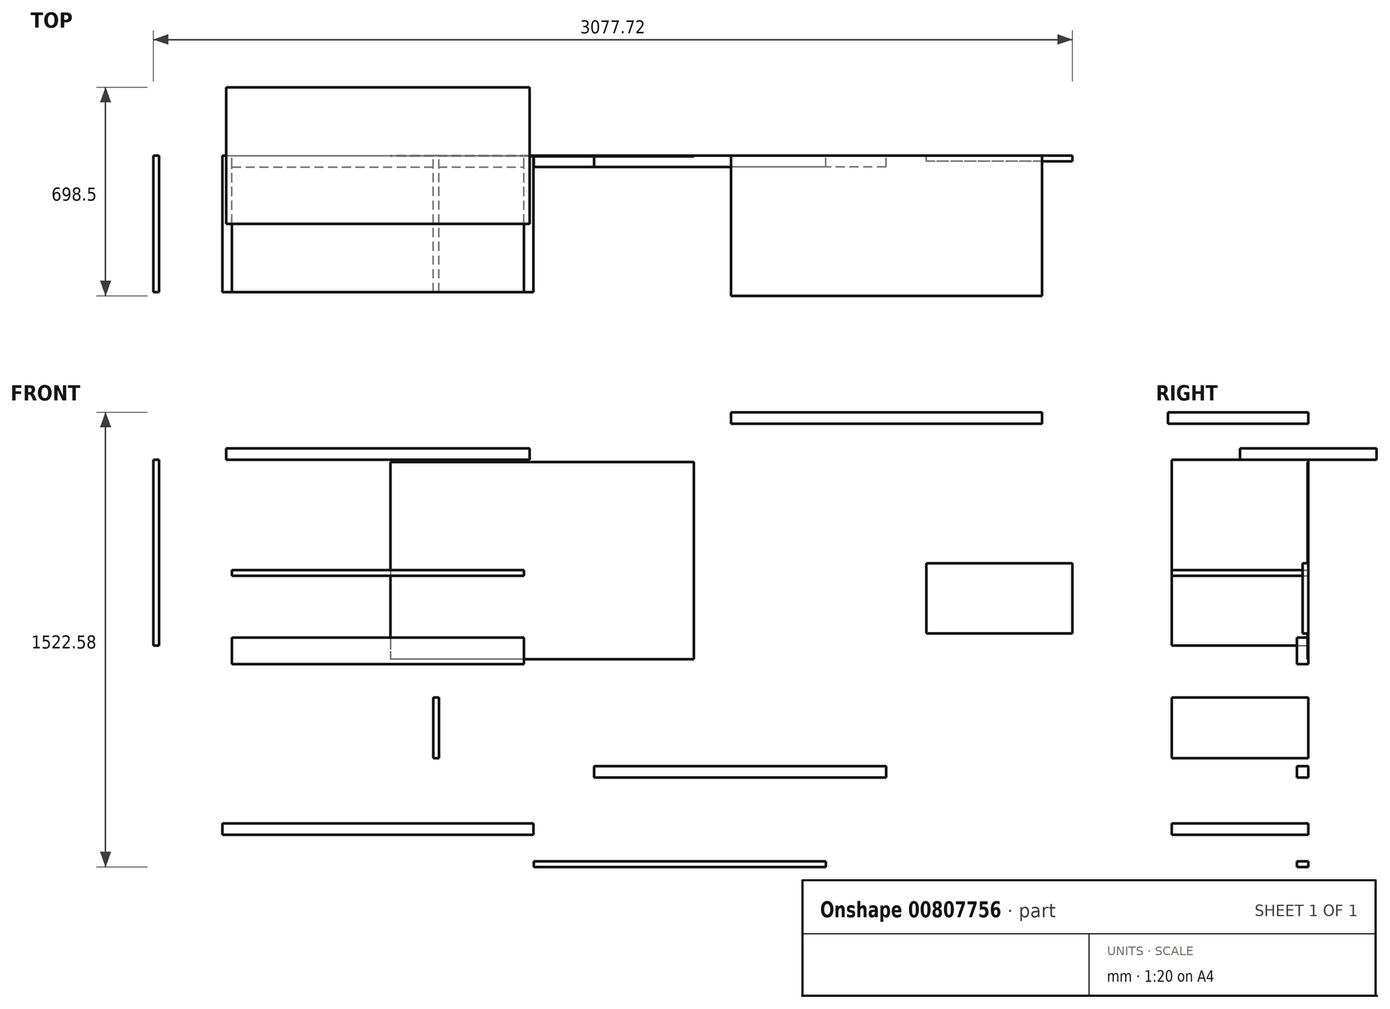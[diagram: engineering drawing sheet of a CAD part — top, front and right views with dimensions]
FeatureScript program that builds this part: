
annotation { "Feature Type Name" : "Feature", "Feature Type Description" : "" }
export const myFeature = defineFeature(function(context is Context, id is Id, definition is map)
    precondition{}
    {
        {
            var Q0;
            Q0=qCreatedBy(makeId("Top.planeOp"),FACE);
            var sketch = newSketch(context, id + "F0", { "sketchPlane" : qUnion([Q0])});
            skLineSegment(sketch, "E0.bottom", {"start": v(508, 228.6) * mm, "end": v(-508, 228.6) * mm});
            skLineSegment(sketch, "E0.top", {"start": v(508, -228.6) * mm, "end": v(-508, -228.6) * mm});
            skLineSegment(sketch, "E0.left", {"start": v(508, 228.6) * mm, "end": v(508, -228.6) * mm});
            skLineSegment(sketch, "E0.right", {"start": v(-508, 228.6) * mm, "end": v(-508, -228.6) * mm});
            skPoint(sketch, "E0.middle", {"position": v(0, 0) * mm});
            skSolve(sketch);
        }
        {
            var Q0;
            Q0 = qSketchRegion(id + "F0", true);
            extrude(context, id + "F1", {"entities" : qUnion([Q0]), "depth" : 38.1 * mm, "offsetDistance" : 25.4 * mm});
        }
        {
            var Q0;
            Q0=qCreatedBy(makeId("Front.planeOp"),FACE);
            var sketch = newSketch(context, id + "F2", { "sketchPlane" : qUnion([Q0])});
            skLineSegment(sketch, "E1.bottom", {"start": v(-752.27, 0) * mm, "end": v(-733.22, 0) * mm});
            skLineSegment(sketch, "E1.top", {"start": v(-752.27, -622.3) * mm, "end": v(-733.22, -622.3) * mm});
            skLineSegment(sketch, "E1.left", {"start": v(-752.27, 0) * mm, "end": v(-752.27, -622.3) * mm});
            skLineSegment(sketch, "E1.right", {"start": v(-733.22, 0) * mm, "end": v(-733.22, -622.3) * mm});
            skSolve(sketch);
        }
        {
            var Q0;
            Q0 = qSketchRegion(id + "F2", true);
            extrude(context, id + "F3", {"entities" : qUnion([Q0]), "depth" : 457.2 * mm, "offsetDistance" : 25.4 * mm});
        }
        {
            var Q0;
            Q0=qCreatedBy(makeId("Front.planeOp"),FACE);
            var sketch = newSketch(context, id + "F4", { "sketchPlane" : qUnion([Q0])});
            skLineSegment(sketch, "E2.bottom", {"start": v(-488.95, -369.1) * mm, "end": v(488.95, -369.1) * mm});
            skLineSegment(sketch, "E2.top", {"start": v(-488.95, -388.14) * mm, "end": v(488.95, -388.14) * mm});
            skLineSegment(sketch, "E2.left", {"start": v(-488.95, -369.1) * mm, "end": v(-488.95, -388.14) * mm});
            skLineSegment(sketch, "E2.right", {"start": v(488.95, -369.1) * mm, "end": v(488.95, -388.14) * mm});
            skPoint(sketch, "E2.middle", {"position": v(0, -378.62) * mm});
            skSolve(sketch);
        }
        {
            var Q0;
            Q0 = qSketchRegion(id + "F4", true);
            extrude(context, id + "F5", {"entities" : qUnion([Q0]), "depth" : 457.2 * mm, "offsetDistance" : 25.4 * mm});
        }
        {
            var Q0;
            Q0=qCreatedBy(makeId("Front.planeOp"),FACE);
            var sketch = newSketch(context, id + "F6", { "sketchPlane" : qUnion([Q0])});
            skLineSegment(sketch, "E3.bottom", {"start": v(-488.95, -595.4) * mm, "end": v(488.95, -595.4) * mm});
            skLineSegment(sketch, "E3.top", {"start": v(-488.95, -684.3) * mm, "end": v(488.95, -684.3) * mm});
            skLineSegment(sketch, "E3.left", {"start": v(-488.95, -595.4) * mm, "end": v(-488.95, -684.3) * mm});
            skLineSegment(sketch, "E3.right", {"start": v(488.95, -595.4) * mm, "end": v(488.95, -684.3) * mm});
            skPoint(sketch, "E3.middle", {"position": v(0, -639.85) * mm});
            skSolve(sketch);
        }
        {
            var Q0;
            Q0 = qSketchRegion(id + "F6", true);
            extrude(context, id + "F7", {"entities" : qUnion([Q0]), "depth" : 38.1 * mm, "offsetDistance" : 25.4 * mm});
        }
        {
            var Q0;
            Q0=qCreatedBy(makeId("Front.planeOp"),FACE);
            var sketch = newSketch(context, id + "F8", { "sketchPlane" : qUnion([Q0])});
            skLineSegment(sketch, "E4.bottom", {"start": v(1057.42, -7.03) * mm, "end": v(41.42, -7.03) * mm});
            skLineSegment(sketch, "E4.top", {"start": v(1057.42, -667.43) * mm, "end": v(41.42, -667.43) * mm});
            skLineSegment(sketch, "E4.left", {"start": v(1057.42, -7.03) * mm, "end": v(1057.42, -667.43) * mm});
            skLineSegment(sketch, "E4.right", {"start": v(41.42, -7.03) * mm, "end": v(41.42, -667.43) * mm});
            skPoint(sketch, "E4.middle", {"position": v(549.42, -337.23) * mm});
            skSolve(sketch);
        }
        {
            var Q0;
            Q0=makeQuery(id+"F8.imprint","IMPRINT",FACE,{"disambiguationData":[TD([[makeQuery(id+"F8.imprint","IMPRINT",EDGE,{"derivedFrom":sQuery(id+"F8.wireOp",EDGE,"E4.bottom")}),1.0]])]});
            extrude(context, id + "F9", {"entities" : qUnion([Q0]), "depth" : 2.54 * mm, "offsetDistance" : 25.4 * mm});
        }
        {
            var Q0;
            Q0=qCreatedBy(makeId("Front.planeOp"),FACE);
            var sketch = newSketch(context, id + "F10", { "sketchPlane" : qUnion([Q0])});
            skLineSegment(sketch, "E5.bottom", {"start": v(203.4, -795.67) * mm, "end": v(184.35, -795.67) * mm});
            skLineSegment(sketch, "E5.top", {"start": v(203.4, -998.87) * mm, "end": v(184.35, -998.87) * mm});
            skLineSegment(sketch, "E5.left", {"start": v(203.4, -795.67) * mm, "end": v(203.4, -998.87) * mm});
            skLineSegment(sketch, "E5.right", {"start": v(184.35, -795.67) * mm, "end": v(184.35, -998.87) * mm});
            skPoint(sketch, "E5.middle", {"position": v(193.87, -897.27) * mm});
            skSolve(sketch);
        }
        {
            var Q0;
            Q0 = qSketchRegion(id + "F10", true);
            extrude(context, id + "F11", {"entities" : qUnion([Q0]), "depth" : 457.2 * mm, "offsetDistance" : 25.4 * mm});
        }
        {
            var Q0;
            Q0=qCreatedBy(makeId("Front.planeOp"),FACE);
            var sketch = newSketch(context, id + "F12", { "sketchPlane" : qUnion([Q0])});
            skLineSegment(sketch, "E6.bottom", {"start": v(-520.7, -1218.14) * mm, "end": v(520.7, -1218.14) * mm});
            skLineSegment(sketch, "E6.top", {"start": v(-520.7, -1256.24) * mm, "end": v(520.7, -1256.24) * mm});
            skLineSegment(sketch, "E6.left", {"start": v(-520.7, -1218.14) * mm, "end": v(-520.7, -1256.24) * mm});
            skLineSegment(sketch, "E6.right", {"start": v(520.7, -1218.14) * mm, "end": v(520.7, -1256.24) * mm});
            skPoint(sketch, "E6.middle", {"position": v(0, -1237.2) * mm});
            skSolve(sketch);
        }
        {
            var Q0;
            Q0 = qSketchRegion(id + "F12", true);
            extrude(context, id + "F13", {"entities" : qUnion([Q0]), "depth" : 457.2 * mm, "offsetDistance" : 25.4 * mm});
        }
        {
            var Q0;
            Q0=qCreatedBy(makeId("Front.planeOp"),FACE);
            var sketch = newSketch(context, id + "F14", { "sketchPlane" : qUnion([Q0])});
            skLineSegment(sketch, "E7.bottom", {"start": v(1700.75, -1025.8) * mm, "end": v(722.85, -1025.8) * mm});
            skLineSegment(sketch, "E7.top", {"start": v(1700.75, -1063.9) * mm, "end": v(722.85, -1063.9) * mm});
            skLineSegment(sketch, "E7.left", {"start": v(1700.75, -1025.8) * mm, "end": v(1700.75, -1063.9) * mm});
            skLineSegment(sketch, "E7.right", {"start": v(722.85, -1025.8) * mm, "end": v(722.85, -1063.9) * mm});
            skPoint(sketch, "E7.middle", {"position": v(1211.8, -1044.85) * mm});
            skSolve(sketch);
        }
        {
            var Q0;
            Q0 = qSketchRegion(id + "F14", true);
            extrude(context, id + "F15", {"entities" : qUnion([Q0]), "depth" : 38.1 * mm, "offsetDistance" : 25.4 * mm});
        }
        {
            var Q0;
            Q0=qCreatedBy(makeId("Front.planeOp"),FACE);
            var sketch = newSketch(context, id + "F16", { "sketchPlane" : qUnion([Q0])});
            skLineSegment(sketch, "E8.bottom", {"start": v(1499.63, -1344.4) * mm, "end": v(521.73, -1344.4) * mm});
            skLineSegment(sketch, "E8.top", {"start": v(1499.63, -1363.45) * mm, "end": v(521.73, -1363.45) * mm});
            skLineSegment(sketch, "E8.left", {"start": v(1499.63, -1344.4) * mm, "end": v(1499.63, -1363.45) * mm});
            skLineSegment(sketch, "E8.right", {"start": v(521.73, -1344.4) * mm, "end": v(521.73, -1363.45) * mm});
            skPoint(sketch, "E8.middle", {"position": v(1010.68, -1353.92) * mm});
            skSolve(sketch);
        }
        {
            var Q0;
            Q0 = qSketchRegion(id + "F16", true);
            extrude(context, id + "F17", {"entities" : qUnion([Q0]), "depth" : 38.1 * mm, "offsetDistance" : 25.4 * mm});
        }
        {
            var Q0;
            Q0=qCreatedBy(makeId("Front.planeOp"),FACE);
            var sketch = newSketch(context, id + "F18", { "sketchPlane" : qUnion([Q0])});
            skLineSegment(sketch, "E9.bottom", {"start": v(2325.45, -581.74) * mm, "end": v(1836.5, -581.74) * mm});
            skLineSegment(sketch, "E9.top", {"start": v(2325.45, -346.8) * mm, "end": v(1836.5, -346.8) * mm});
            skLineSegment(sketch, "E9.left", {"start": v(2325.45, -581.74) * mm, "end": v(2325.45, -346.8) * mm});
            skLineSegment(sketch, "E9.right", {"start": v(1836.5, -581.74) * mm, "end": v(1836.5, -346.8) * mm});
            skPoint(sketch, "E9.middle", {"position": v(2080.98, -464.27) * mm});
            skSolve(sketch);
        }
        {
            var Q0;
            Q0 = qSketchRegion(id + "F18", true);
            extrude(context, id + "F19", {"entities" : qUnion([Q0]), "depth" : 19.05 * mm, "offsetDistance" : 25.4 * mm});
        }
        {
            var Q0;
            Q0=qCreatedBy(makeId("Front.planeOp"),FACE);
            var sketch = newSketch(context, id + "F20", { "sketchPlane" : qUnion([Q0])});
            skLineSegment(sketch, "E10.bottom", {"start": v(2222.85, 159.13) * mm, "end": v(1181.45, 159.13) * mm});
            skLineSegment(sketch, "E10.top", {"start": v(2222.85, 121.03) * mm, "end": v(1181.45, 121.03) * mm});
            skLineSegment(sketch, "E10.left", {"start": v(2222.85, 159.13) * mm, "end": v(2222.85, 121.03) * mm});
            skLineSegment(sketch, "E10.right", {"start": v(1181.45, 159.13) * mm, "end": v(1181.45, 121.03) * mm});
            skPoint(sketch, "E10.middle", {"position": v(1702.15, 140.08) * mm});
            skSolve(sketch);
        }
        {
            var Q0;
            Q0 = qSketchRegion(id + "F20", true);
            extrude(context, id + "F21", {"entities" : qUnion([Q0]), "depth" : 469.9 * mm, "offsetDistance" : 25.4 * mm});
        }
    });
